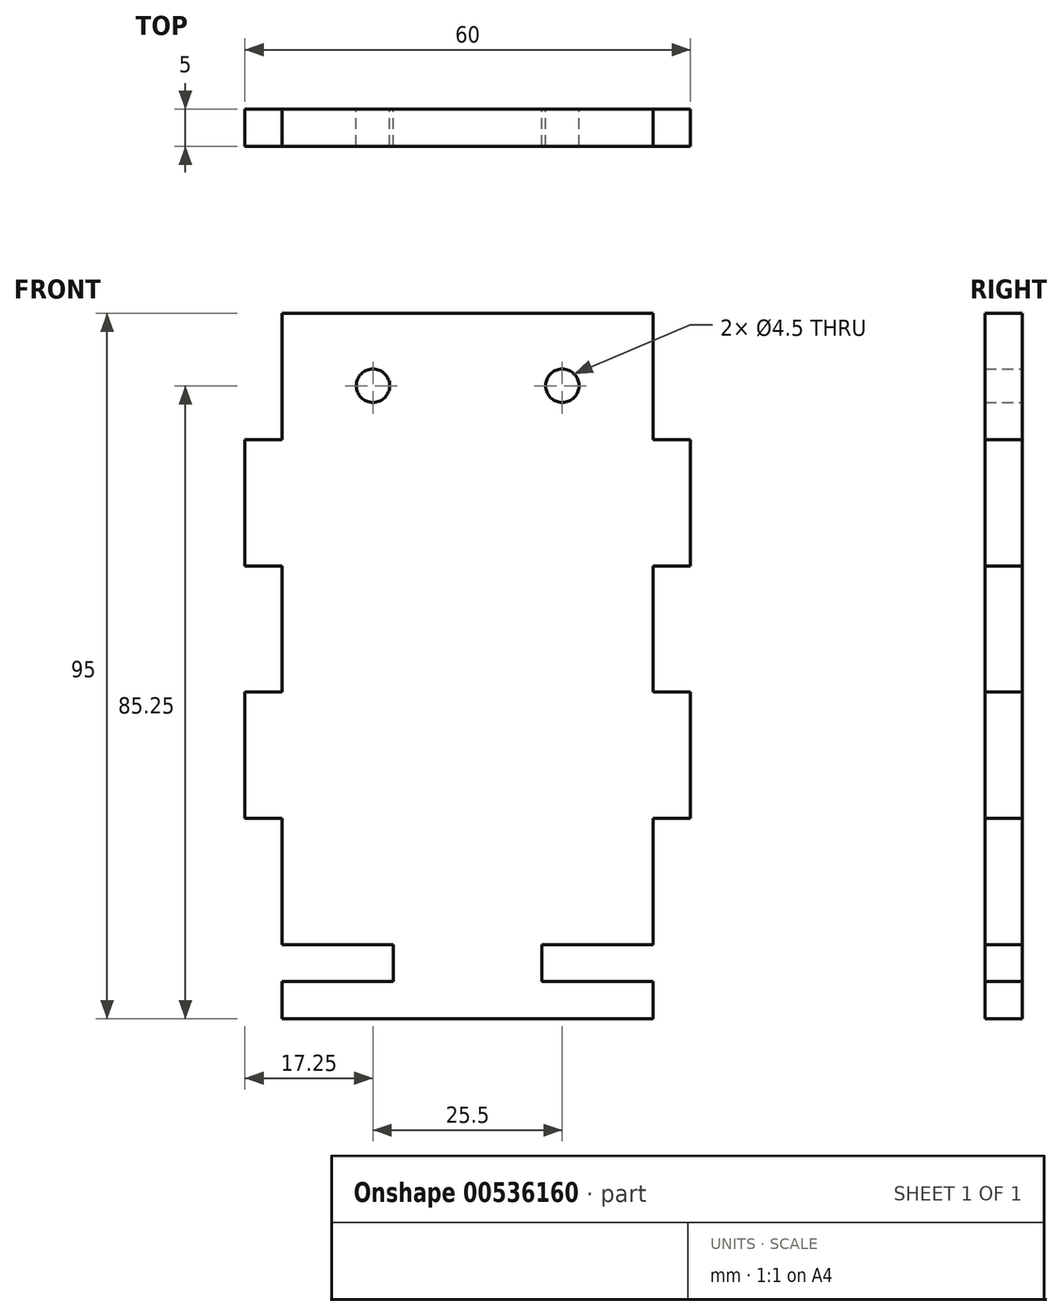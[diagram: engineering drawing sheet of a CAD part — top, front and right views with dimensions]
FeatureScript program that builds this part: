
annotation { "Feature Type Name" : "Feature", "Feature Type Description" : "" }
export const myFeature = defineFeature(function(context is Context, id is Id, definition is map)
    precondition{}
    {
        {
            var Q0;
            Q0=qCreatedBy(makeId("Front.planeOp"),FACE);
            var sketch = newSketch(context, id + "F0", { "sketchPlane" : qUnion([Q0])});
            skLineSegment(sketch, "E0.bottom", {"start": v(25, 42.5) * mm, "end": v(-25, 42.5) * mm});
            skLineSegment(sketch, "E0.top", {"start": v(25, -42.5) * mm, "end": v(10, -42.5) * mm});
            skLineSegment(sketch, "E0.left", {"start": v(25, 42.5) * mm, "end": v(25, 25.5) * mm});
            skLineSegment(sketch, "E0.right", {"start": v(-25, 42.5) * mm, "end": v(-25, 25.5) * mm});
            skPoint(sketch, "E0.middle", {"position": v(0, 0) * mm});
            skLineSegment(sketch, "E1", {"start": v(-30, 42.5) * mm, "end": v(-30, -47.5) * mm, "construction": true});
            skLineSegment(sketch, "E2", {"start": v(-25, -47.5) * mm, "end": v(-10, -47.5) * mm, "construction": true});
            skLineSegment(sketch, "E3", {"start": v(30, -47.5) * mm, "end": v(30, 42.5) * mm, "construction": true});
            skLineSegment(sketch, "E4", {"start": v(-10, -42.5) * mm, "end": v(-10, -47.5) * mm});
            skLineSegment(sketch, "E5", {"start": v(-10, -47.5) * mm, "end": v(-25, -47.5) * mm});
            skLineSegment(sketch, "E6", {"start": v(-25, -52.5) * mm, "end": v(25, -52.5) * mm});
            skLineSegment(sketch, "E7", {"start": v(10, -42.5) * mm, "end": v(10, -47.5) * mm});
            skLineSegment(sketch, "E8", {"start": v(10, -47.5) * mm, "end": v(30, -47.5) * mm});
            skLineSegment(sketch, "E9", {"start": v(-25, -25.5) * mm, "end": v(-30, -25.5) * mm});
            skLineSegment(sketch, "E10", {"start": v(-30, -25.5) * mm, "end": v(-30, -8.5) * mm});
            skLineSegment(sketch, "E11", {"start": v(-30, -8.5) * mm, "end": v(-25, -8.5) * mm});
            skLineSegment(sketch, "E12", {"start": v(-25, 8.5) * mm, "end": v(-30, 8.5) * mm});
            skLineSegment(sketch, "E13", {"start": v(-30, 8.5) * mm, "end": v(-30, 25.5) * mm});
            skLineSegment(sketch, "E14", {"start": v(-30, 25.5) * mm, "end": v(-25, 25.5) * mm});
            skLineSegment(sketch, "E15.trimOffspring", {"start": v(-25, 8.5) * mm, "end": v(-25, -8.5) * mm});
            skLineSegment(sketch, "E16.trimOffspring", {"start": v(-25, -25.5) * mm, "end": v(-25, -42.5) * mm});
            skLineSegment(sketch, "E17.MirrorCS", {"start": v(30, 25.5) * mm, "end": v(25, 25.5) * mm});
            skLineSegment(sketch, "E18.MirrorCS", {"start": v(25, 8.5) * mm, "end": v(30, 8.5) * mm});
            skLineSegment(sketch, "E19.MirrorCS", {"start": v(30, -8.5) * mm, "end": v(25, -8.5) * mm});
            skLineSegment(sketch, "E20.MirrorCS", {"start": v(25, -25.5) * mm, "end": v(30, -25.5) * mm});
            skLineSegment(sketch, "E21", {"start": v(30, 25.5) * mm, "end": v(30, 8.5) * mm});
            skLineSegment(sketch, "E22", {"start": v(30, -8.5) * mm, "end": v(30, -25.5) * mm});
            skLineSegment(sketch, "E23.trimOffspring", {"start": v(25, 8.5) * mm, "end": v(25, -8.5) * mm});
            skLineSegment(sketch, "E24.trimOffspring", {"start": v(25, -25.5) * mm, "end": v(25, -42.5) * mm});
            skLineSegment(sketch, "E25.trimOffspring", {"start": v(-10, -42.5) * mm, "end": v(-25, -42.5) * mm});
            skLineSegment(sketch, "E26.trimOffspring", {"start": v(10, -47.5) * mm, "end": v(25, -47.5) * mm, "construction": true});
            skLineSegment(sketch, "E27", {"start": v(-25, -47.5) * mm, "end": v(-25, -52.5) * mm});
            skLineSegment(sketch, "E28", {"start": v(25, -47.5) * mm, "end": v(25, -52.5) * mm});
            skPoint(sketch, "E29.start.orphan", {"position": v(30, -52.5) * mm});
            skLineSegment(sketch, "E30.bottom", {"start": v(17.5, 56.5) * mm, "end": v(-17.5, 56.5) * mm, "construction": true});
            skLineSegment(sketch, "E30.top", {"start": v(17.5, 28.5) * mm, "end": v(-17.5, 28.5) * mm, "construction": true});
            skLineSegment(sketch, "E30.left", {"start": v(17.5, 56.5) * mm, "end": v(17.5, 28.5) * mm, "construction": true});
            skLineSegment(sketch, "E30.right", {"start": v(-17.5, 56.5) * mm, "end": v(-17.5, 28.5) * mm, "construction": true});
            skPoint(sketch, "E30.middle", {"position": v(0, 42.5) * mm});
            skCircle(sketch, "E31", {"center": v(-12.75, 32.75) * mm, "radius": 2.25 * mm});
            skCircle(sketch, "E32", {"center": v(12.75, 32.75) * mm, "radius": 2.25 * mm});
            skSolve(sketch);
        }
        {
            var Q0;
            Q0 = qSketchRegion(id + "F0", true);
            extrude(context, id + "F1", {"entities" : qUnion([Q0]), "depth" : 5 * mm, "offsetDistance" : 25 * mm});
        }
    });
